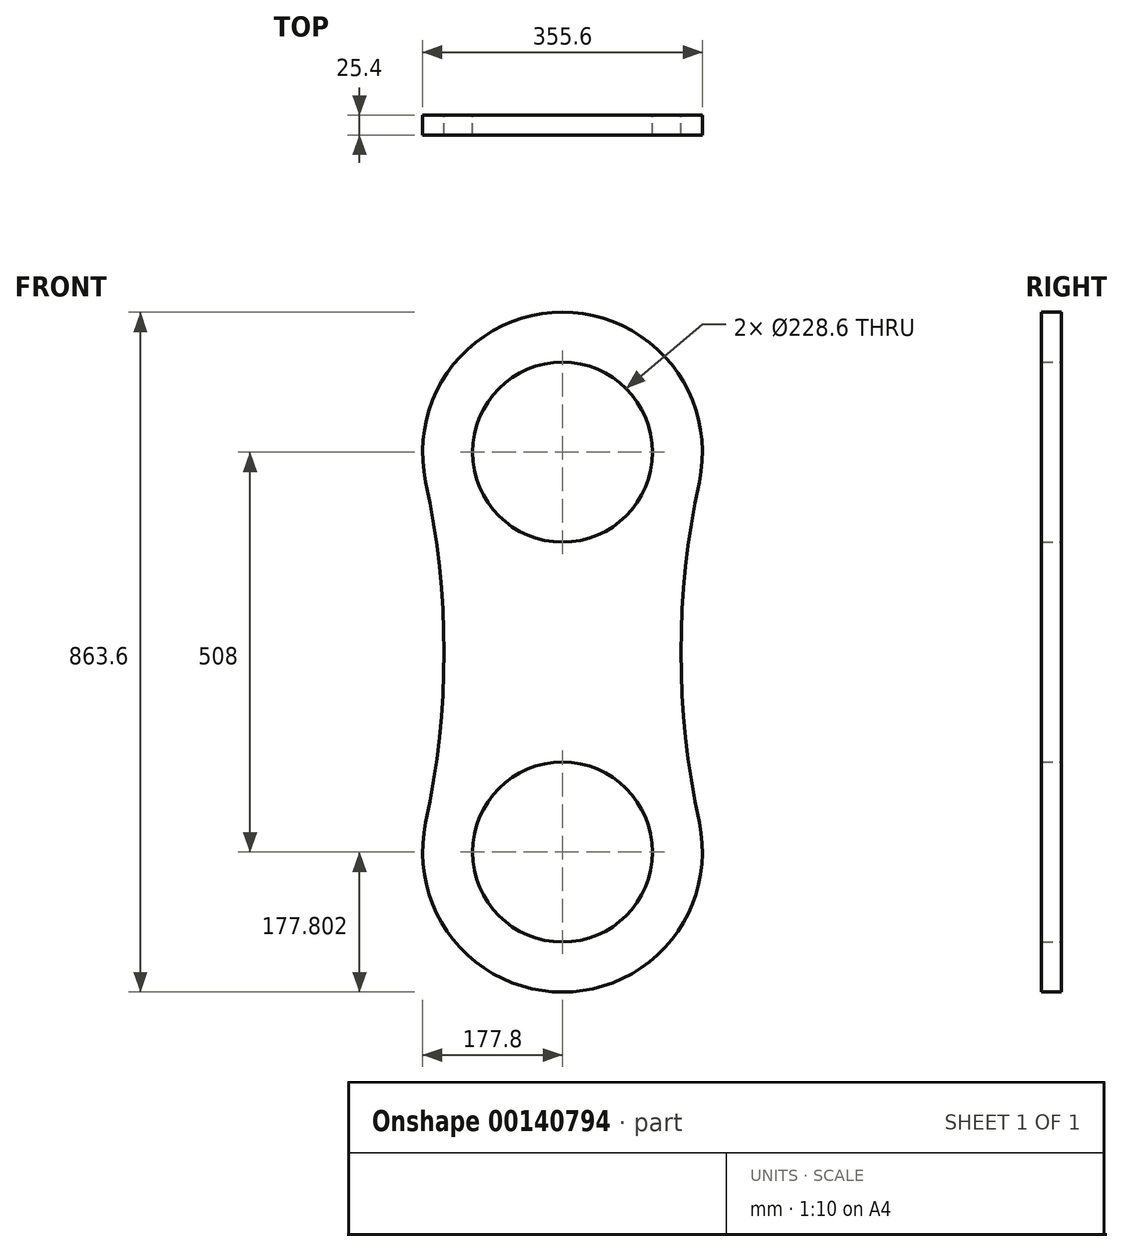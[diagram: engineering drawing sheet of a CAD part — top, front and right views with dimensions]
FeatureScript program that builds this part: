
annotation { "Feature Type Name" : "Feature", "Feature Type Description" : "" }
export const myFeature = defineFeature(function(context is Context, id is Id, definition is map)
    precondition{}
    {
        {
            var Q0;
            Q0=qCreatedBy(makeId("Front.planeOp"),FACE);
            var sketch = newSketch(context, id + "F0", { "sketchPlane" : qUnion([Q0])});
            skArc(sketch, "E0", {"start": v(173.73, 176.11) * mm, "mid": v(0, 391.74) * mm, "end": v(-173.73, 176.11) * mm});
            skArc(sketch, "E1", {"start": v(-173.73, -256.23) * mm, "mid": v(0, -471.86) * mm, "end": v(173.73, -256.23) * mm});
            skArc(sketch, "E2", {"start": v(-173.73, -256.23) * mm, "mid": v(-150.47, -40.06) * mm, "end": v(-173.73, 176.11) * mm});
            skArc(sketch, "E3", {"start": v(173.73, 176.11) * mm, "mid": v(150.47, -40.06) * mm, "end": v(173.73, -256.23) * mm});
            skCircle(sketch, "E4", {"center": v(0, 213.94) * mm, "radius": 114.3 * mm});
            skCircle(sketch, "E5", {"center": v(0, -294.06) * mm, "radius": 114.3 * mm});
            skSolve(sketch);
        }
        {
            var Q0;
            Q0=makeQuery(id+"F0.imprint","IMPRINT",FACE,{"disambiguationData":[TD([[makeQuery(id+"F0.imprint","IMPRINT",EDGE,{"derivedFrom":sQuery(id+"F0.wireOp",EDGE,"E0")}),1.0]])]});
            extrude(context, id + "F1", {"entities" : qUnion([Q0]), "depth" : 25.4 * mm});
        }
    });
